# Revit family: LAMP_B-SIDE 360 250
name_source: partatom
category: Luminarias
revit_build: Autodesk Revit LT 2015 (Build: 20140606_1530(x64)
units: mm (PartAtom-declared; Revit-internal decimal feet)

## types (2) — shared parameters
CRI = 80
Cambio de temperatura de color de luz atenuada = <Ninguno>
Diameter = 160 mm  [stored 0.524934 ft]
Efficacy = 45 lm/W
Elevación por defecto = 1219 mm
Fabricante = LAMP
Filtro de color = 16777215
Gear = Electronic
Height = 250 mm  [stored 0.82021 ft]
IEE = A++
Installation instructions = https://www.lamp.es
Insulation class = I
LED Lifetime = 50000 L90 B10
Last update = 21/12/2020
Luminaire type = Outdoor - Beacon
Lámpara = COB LED
MacAdam = 3
Manufacturer URL = http://www.lamp.es
Manufacturer country = Spain
Manufacturer name = LAMP
Material cristal = LAMP_Cristal B-Side Transparente
Plum = 10 W
Power = 8 W
Power Supply = 220-240V 50-60Hz
Product URL = https://www.lamp.es
Product datasheet = http://www.lamp.es
Protection rating = IP65 / IK06
Type = COB PHILIPS
Weight = 3.62 kg
Ángulo de inclinación = 90.00°

## per-type parameters (varying)
| type | Archivo de red fotométrica | Descripción | Finish | Material | Modelo | Product code |
| 451LM 4000 BLACK | 5841344.IES | B-SIDE 360º LED 250 1000 NW ANT. | Textured anthracite grey | LAMP_Aluminio B-Side antracita | BS1RD2510840NA | BS1RD2510840NA |
| 451LM 4000 GREY | 5841343.IES | B-SIDE 360º LED 250 1000 NW GR. | Texturised grey | LAMP_Aluminio B-Side gris | BS1RD2510840NG | BS1RD2510840NG |

note: [stored X ft] marks values corroborated as IEEE doubles in the binary element streams (Revit-internal decimal feet)
